# Revit family: LAMP_MAINS SUPPLY 48V
name_source: partatom
category: Mobiliario
revit_build: Autodesk Revit 2015 (Build: 20140606_1530(x64)
units: mm (PartAtom-declared; Revit-internal decimal feet)

## types (4) — shared parameters
Accessory Type = Assembly
Fabricante = LAMP
Installation instructions = https://www.lamp.es
Last update = 29/03/2019
Manufacturer URL = http://www.lamp.es
Manufacturer country = Spain
Manufacturer name = LAMP
Product URL = https://www.lamp.es
Product datasheet = http://www.lamp.es
Weight = 0.15 kg

## per-type parameters (varying)
| type | Descripción | Finish | Material | Modelo | Product code |
| LEFT BLACK | TRACK 48V ACC. LEFT MAIN SUPPLY DALI BK. | RAL9011 textured | LAMP_Aluminio Carril NG | TLSUALDB | TLSUALDB |
| LEFT WHITE | TRACK 48V ACC. LEFT MAIN SUPPLY DALI WH. | RAL9010 textured | LAMP_Aluminio Carril BL | TLSUALDW | TLSUALDW |
| RIGHT BLACK | TRACK 48V ACC. RIGHT MAIN SUPPLY DALI BK | RAL9011 textured | LAMP_Aluminio Carril NG | TLSUARDB | TLSUARDB |
| RIGHT WHITE | TRACK 48V ACC. RIGHT MAIN SUPPLY DALI WH | RAL9010 textured | LAMP_Aluminio Carril BL | TLSUARDW | TLSUARDW |
